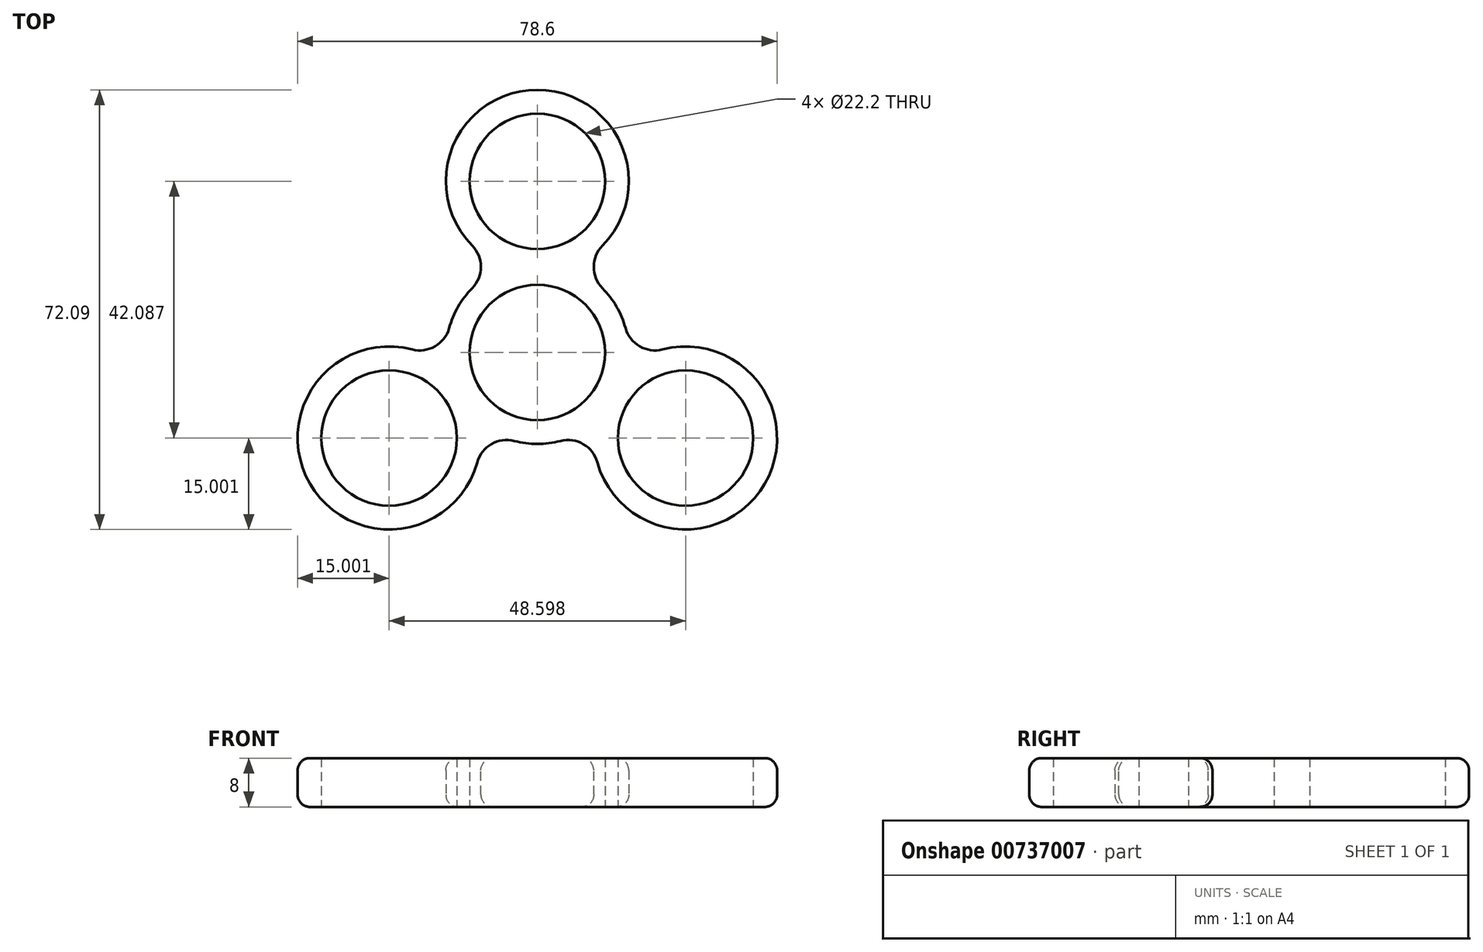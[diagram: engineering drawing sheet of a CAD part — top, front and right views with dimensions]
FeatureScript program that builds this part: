
annotation { "Feature Type Name" : "Feature", "Feature Type Description" : "" }
export const myFeature = defineFeature(function(context is Context, id is Id, definition is map)
    precondition{}
    {
        {
            var Q0;
            Q0=qCreatedBy(makeId("Top.planeOp"),FACE);
            var sketch = newSketch(context, id + "F0", { "sketchPlane" : qUnion([Q0])});
            skCircle(sketch, "E0", {"center": v(0, 0) * mm, "radius": 11.1 * mm});
            skCircle(sketch, "E1", {"center": v(0, 28.06) * mm, "radius": 11.1 * mm});
            skCircle(sketch, "E2", {"center": v(0, 0) * mm, "radius": 15 * mm});
            skCircle(sketch, "E3", {"center": v(0, 28.06) * mm, "radius": 15 * mm});
            skSolve(sketch);
        }
        {
            var Q0;
            Q0=makeQuery(id+"F0.imprint","IMPRINT",FACE,{"disambiguationData":[TD([[makeQuery(id+"F0.imprint","IMPRINT",EDGE,{"derivedFrom":sQuery(id+"F0.wireOp",EDGE,"E0")}),-1.0]])]});
            var Q1;
            {var subQ3=sQuery(id+"F0.wireOp",EDGE,"4vwqms1l-6MHH-CEMi-Rsp6-VB6GKGdyafBa");Q1=makeQuery(id+"F0.imprint","IMPRINT",FACE,{"disambiguationData":[TD([[makeQuery(id+"F0.imprint","IMPRINT",EDGE,{"derivedFrom":subQ3}),1.0]])]});}
            var Q2;
            Q2=makeQuery(id+"F0.imprint","IMPRINT",FACE,{"disambiguationData":[TD([[makeQuery(id+"F0.imprint","IMPRINT",EDGE,{"derivedFrom":sQuery(id+"F0.wireOp",EDGE,"E1")}),-1.0]])]});
            extrude(context, id + "F1", {"entities" : qUnion([Q0, Q1, Q2]), "depth" : 8 * mm, "offsetDistance" : 25 * mm});
        }
        {
            var Q0;
            Q0=makeQuery(id+"F1.opExtrude","SWEPT_BODY",BODY,{"disambiguationData":[OSD([sQuery(id+"F0.wireOp",EDGE,"E0"),sQuery(id+"F0.wireOp",EDGE,"E1"),sQuery(id+"F0.wireOp",EDGE,"E2"),sQuery(id+"F0.wireOp",EDGE,"E3"),sQuery(id+"F0.wireOp",EDGE,"DIWTCUvn-fpTy-xWw9-RbGA-DcyN7KAXeMk2"),sQuery(id+"F0.wireOp",EDGE,"4vwqms1l-6MHH-CEMi-Rsp6-VB6GKGdyafBa")])]});
            var Q1;
            Q1=makeQuery(id+"F1.opExtrude","CAP_EDGE",EDGE,{"disambiguationData":[OSD([sQuery(id+"F0.wireOp",EDGE,"E0")])],"isStart":false});
            circularPattern(context, id + "F2", {"entities" : qUnion([Q0]), "axis" : qUnion([Q1]), "angle" : 360 * degree, "instanceCount" : 3, "equalSpace" : true});
        }
        {
            var Q0;
            Q0=makeQuery(id+"F1.opExtrude","SWEPT_BODY",BODY,{"disambiguationData":[OSD([sQuery(id+"F0.wireOp",EDGE,"E0"),sQuery(id+"F0.wireOp",EDGE,"E1"),sQuery(id+"F0.wireOp",EDGE,"E2"),sQuery(id+"F0.wireOp",EDGE,"E3"),sQuery(id+"F0.wireOp",EDGE,"DIWTCUvn-fpTy-xWw9-RbGA-DcyN7KAXeMk2"),sQuery(id+"F0.wireOp",EDGE,"4vwqms1l-6MHH-CEMi-Rsp6-VB6GKGdyafBa")])]});
            var Q1;
            Q1=makeQuery(id+"F2.opPattern","COPY",BODY,{"derivedFrom":makeQuery(id+"F1.opExtrude","SWEPT_BODY",BODY,{"disambiguationData":[OSD([sQuery(id+"F0.wireOp",EDGE,"E0"),sQuery(id+"F0.wireOp",EDGE,"E1"),sQuery(id+"F0.wireOp",EDGE,"E2"),sQuery(id+"F0.wireOp",EDGE,"E3"),sQuery(id+"F0.wireOp",EDGE,"DIWTCUvn-fpTy-xWw9-RbGA-DcyN7KAXeMk2"),sQuery(id+"F0.wireOp",EDGE,"4vwqms1l-6MHH-CEMi-Rsp6-VB6GKGdyafBa")])]}),"instanceName":"2"});
            var Q2;
            Q2=makeQuery(id+"F2.opPattern","COPY",BODY,{"derivedFrom":makeQuery(id+"F1.opExtrude","SWEPT_BODY",BODY,{"disambiguationData":[OSD([sQuery(id+"F0.wireOp",EDGE,"E0"),sQuery(id+"F0.wireOp",EDGE,"E1"),sQuery(id+"F0.wireOp",EDGE,"E2"),sQuery(id+"F0.wireOp",EDGE,"E3"),sQuery(id+"F0.wireOp",EDGE,"DIWTCUvn-fpTy-xWw9-RbGA-DcyN7KAXeMk2"),sQuery(id+"F0.wireOp",EDGE,"4vwqms1l-6MHH-CEMi-Rsp6-VB6GKGdyafBa")])]}),"instanceName":"1"});
            booleanBodies(context, id + "F3", {"operationType" : BooleanOperationType.UNION, "tools" : qUnion([Q0, Q1, Q2])});
        }
        {
            var Q0;
            {var subQ0=sQuery(id+"F0.wireOp",EDGE,"E3");var subQ1=sQuery(id+"F0.wireOp",EDGE,"E2");var subQ2=makeQuery(id+"F0.imprint","INTERSECT",VERTEX,{"disambiguationData":[OD(0.0)],"derivedFrom":[subQ1,subQ0]});Q0=makeQuery(id+"F3.opBoolean","MERGE",EDGE,{"derivedFrom":[makeQuery(id+"F1.opExtrude","SWEPT_EDGE",EDGE,{"disambiguationData":[OSD([subQ1,subQ0]),TDD([subQ2]),OD(0.0)]}),makeQuery(id+"F1.opExtrude","SWEPT_EDGE",EDGE,{"disambiguationData":[OSD([subQ1,subQ0]),TDD([subQ2]),OD(1.0)]})]});}
            var Q1;
            {var subQ0=sQuery(id+"F0.wireOp",EDGE,"E3");var subQ1=sQuery(id+"F0.wireOp",EDGE,"E2");var subQ2=makeQuery(id+"F0.imprint","INTERSECT",VERTEX,{"disambiguationData":[OD(1.0)],"derivedFrom":[subQ1,subQ0]});Q1=makeQuery(id+"F3.opBoolean","MERGE",EDGE,{"derivedFrom":[makeQuery(id+"F1.opExtrude","SWEPT_EDGE",EDGE,{"disambiguationData":[OSD([subQ1,subQ0]),TDD([subQ2]),OD(0.0)]}),makeQuery(id+"F1.opExtrude","SWEPT_EDGE",EDGE,{"disambiguationData":[OSD([subQ1,subQ0]),TDD([subQ2]),OD(1.0)]})]});}
            var Q2;
            {var subQ0=sQuery(id+"F0.wireOp",EDGE,"E3");var subQ1=sQuery(id+"F0.wireOp",EDGE,"E2");Q2=makeQuery(id+"F2.opPattern","COPY",EDGE,{"derivedFrom":makeQuery(id+"F1.opExtrude","SWEPT_EDGE",EDGE,{"disambiguationData":[OSD([subQ1,subQ0]),TDD([makeQuery(id+"F0.imprint","INTERSECT",VERTEX,{"disambiguationData":[OD(1.0)],"derivedFrom":[subQ1,subQ0]})]),OD(0.0)]}),"instanceName":"1"});}
            var Q3;
            {var subQ0=sQuery(id+"F0.wireOp",EDGE,"E3");var subQ1=sQuery(id+"F0.wireOp",EDGE,"E2");Q3=makeQuery(id+"F2.opPattern","COPY",EDGE,{"derivedFrom":makeQuery(id+"F1.opExtrude","SWEPT_EDGE",EDGE,{"disambiguationData":[OSD([subQ1,subQ0]),TDD([makeQuery(id+"F0.imprint","INTERSECT",VERTEX,{"disambiguationData":[OD(0.0)],"derivedFrom":[subQ1,subQ0]})]),OD(0.0)]}),"instanceName":"1"});}
            var Q4;
            {var subQ0=sQuery(id+"F0.wireOp",EDGE,"E3");var subQ1=sQuery(id+"F0.wireOp",EDGE,"E2");var subQ2=makeQuery(id+"F0.imprint","INTERSECT",VERTEX,{"disambiguationData":[OD(1.0)],"derivedFrom":[subQ1,subQ0]});Q4=makeQuery(id+"F3.opBoolean","MERGE",EDGE,{"derivedFrom":[makeQuery(id+"F2.opPattern","COPY",EDGE,{"derivedFrom":makeQuery(id+"F1.opExtrude","SWEPT_EDGE",EDGE,{"disambiguationData":[OSD([subQ1,subQ0]),TDD([subQ2]),OD(0.0)]}),"instanceName":"2"}),makeQuery(id+"F2.opPattern","COPY",EDGE,{"derivedFrom":makeQuery(id+"F1.opExtrude","SWEPT_EDGE",EDGE,{"disambiguationData":[OSD([subQ1,subQ0]),TDD([subQ2]),OD(1.0)]}),"instanceName":"2"})]});}
            var Q5;
            {var subQ0=sQuery(id+"F0.wireOp",EDGE,"E3");var subQ1=sQuery(id+"F0.wireOp",EDGE,"E2");var subQ2=makeQuery(id+"F0.imprint","INTERSECT",VERTEX,{"disambiguationData":[OD(0.0)],"derivedFrom":[subQ1,subQ0]});Q5=makeQuery(id+"F3.opBoolean","MERGE",EDGE,{"derivedFrom":[makeQuery(id+"F2.opPattern","COPY",EDGE,{"derivedFrom":makeQuery(id+"F1.opExtrude","SWEPT_EDGE",EDGE,{"disambiguationData":[OSD([subQ1,subQ0]),TDD([subQ2]),OD(0.0)]}),"instanceName":"2"}),makeQuery(id+"F2.opPattern","COPY",EDGE,{"derivedFrom":makeQuery(id+"F1.opExtrude","SWEPT_EDGE",EDGE,{"disambiguationData":[OSD([subQ1,subQ0]),TDD([subQ2]),OD(1.0)]}),"instanceName":"2"})]});}
            fillet(context, id + "F4", {"entities" : qUnion([Q0, Q1, Q2, Q3, Q4, Q5]), "radius" : 5 * mm, "tangentPropagation" : true, "allowEdgeOverflow" : false});
        }
        {
            var Q0;
            {var subQ0=sQuery(id+"F0.wireOp",EDGE,"E3");var subQ1=sQuery(id+"F0.wireOp",EDGE,"E2");Q0=makeQuery(id+"F1.opExtrude","CAP_EDGE",EDGE,{"disambiguationData":[OSD([subQ0]),TDD([makeQuery(id+"F0.imprint","IMPRINT",EDGE,{"disambiguationData":[TD([[makeQuery(id+"F0.imprint","INTERSECT",VERTEX,{"disambiguationData":[OD(0.0)],"derivedFrom":[subQ1,subQ0]}),1.0]])],"derivedFrom":subQ0})])],"isStart":false});}
            var Q1;
            {var subQ0=sQuery(id+"F0.wireOp",EDGE,"E3");var subQ1=sQuery(id+"F0.wireOp",EDGE,"E2");Q1=makeQuery(id+"F1.opExtrude","CAP_EDGE",EDGE,{"disambiguationData":[OSD([subQ0]),TDD([makeQuery(id+"F0.imprint","IMPRINT",EDGE,{"disambiguationData":[TD([[makeQuery(id+"F0.imprint","INTERSECT",VERTEX,{"disambiguationData":[OD(0.0)],"derivedFrom":[subQ1,subQ0]}),1.0]])],"derivedFrom":subQ0})])],"isStart":true});}
            fillet(context, id + "F5", {"entities" : qUnion([Q0, Q1]), "radius" : 2 * mm, "tangentPropagation" : true, "allowEdgeOverflow" : false});
        }
    });
